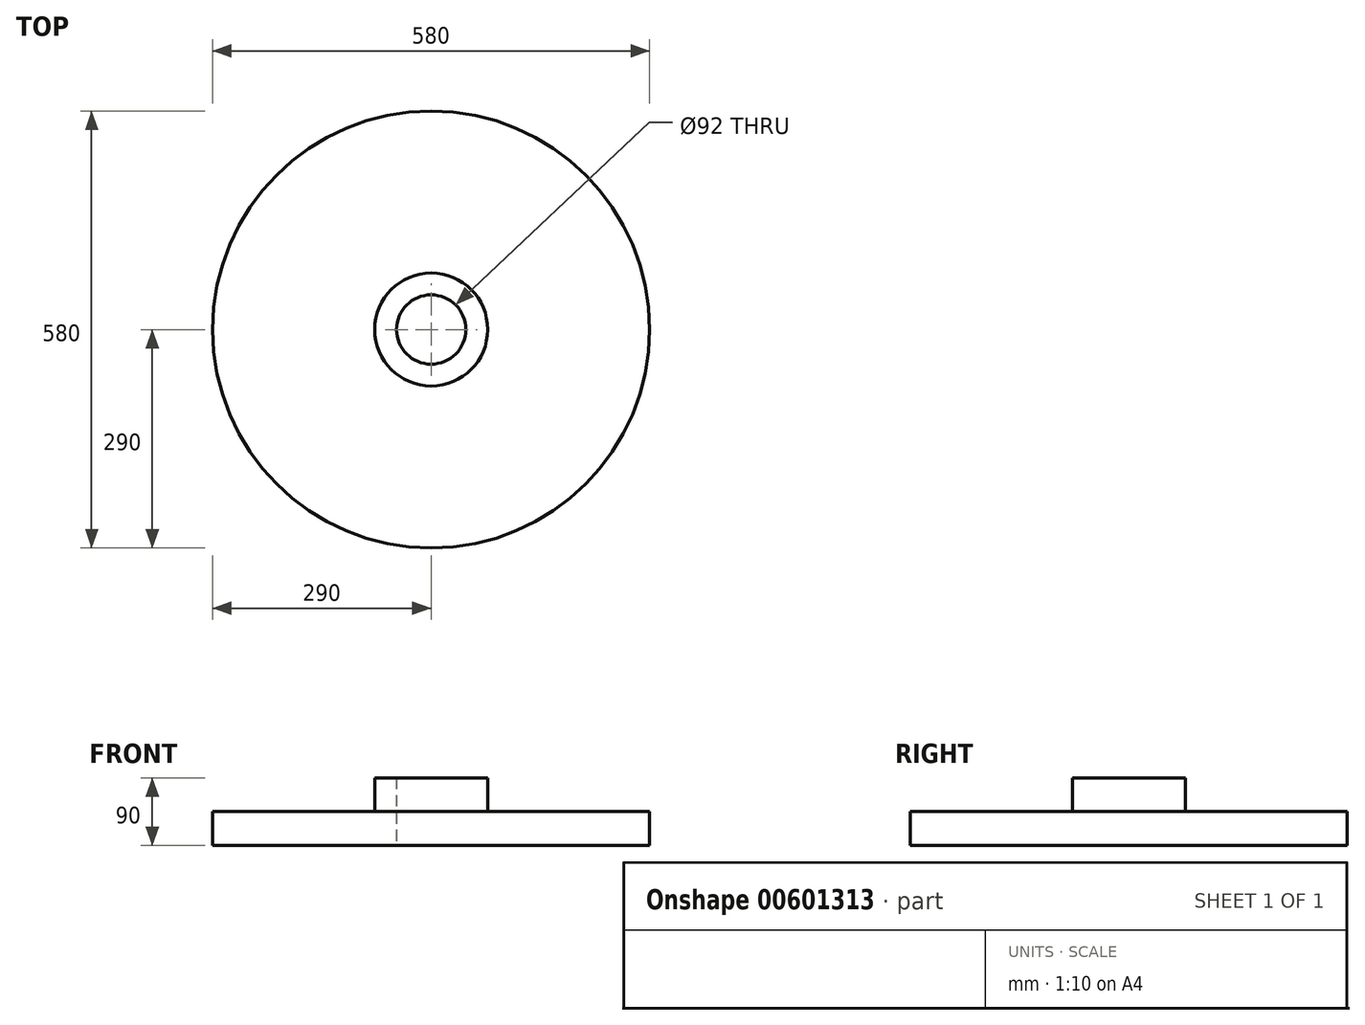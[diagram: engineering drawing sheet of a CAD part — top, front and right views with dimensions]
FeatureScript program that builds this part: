
annotation { "Feature Type Name" : "Feature", "Feature Type Description" : "" }
export const myFeature = defineFeature(function(context is Context, id is Id, definition is map)
    precondition{}
    {
        {
            var Q0;
            Q0=qCreatedBy(makeId("Front.planeOp"),FACE);
            var sketch = newSketch(context, id + "F0", { "sketchPlane" : qUnion([Q0])});
            skLineSegment(sketch, "E0", {"start": v(46, 90) * mm, "end": v(46, 0) * mm});
            skLineSegment(sketch, "E1", {"start": v(46, 0) * mm, "end": v(290, 0) * mm});
            skLineSegment(sketch, "E2", {"start": v(290, 0) * mm, "end": v(290, 45) * mm});
            skLineSegment(sketch, "E3", {"start": v(290, 45) * mm, "end": v(75, 45) * mm});
            skLineSegment(sketch, "E4", {"start": v(75, 45) * mm, "end": v(75, 90) * mm});
            skLineSegment(sketch, "E5", {"start": v(75, 90) * mm, "end": v(46, 90) * mm});
            skLineSegment(sketch, "E6", {"start": v(0, 0) * mm, "end": v(0, 195.12) * mm, "construction": true});
            skSolve(sketch);
        }
        {
            var Q0;
            Q0=makeQuery(id+"F0.imprint","IMPRINT",FACE,{"disambiguationData":[TD([[makeQuery(id+"F0.imprint","IMPRINT",EDGE,{"derivedFrom":sQuery(id+"F0.wireOp",EDGE,"E0")}),1.0]])]});
            var Q1;
            Q1=sQuery(id+"F0.wireOp",EDGE,"E6");
            revolve(context, id + "F1", {"entities" : qUnion([Q0]), "axis" : qUnion([Q1]), "revolveType" : RevolveType.FULL});
        }
    });
